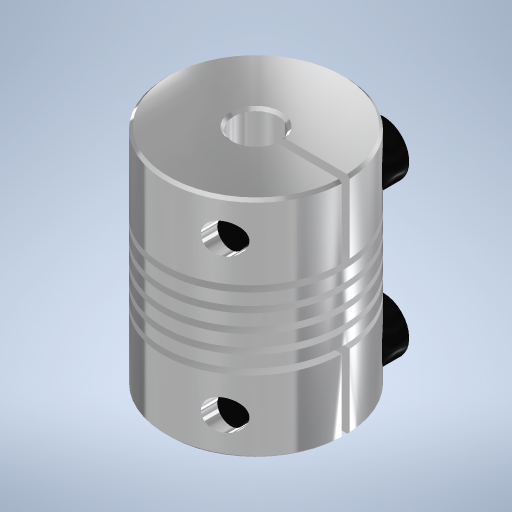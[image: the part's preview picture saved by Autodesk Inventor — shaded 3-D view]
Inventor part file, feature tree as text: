
AUTODESK INVENTOR PART (.ipt)
format: ipt  version: 2024 (Build 280153000, 153)  size: 555,520 bytes
history: native  units: mm
features: extrude x3, sketch x3, projected_geometry x2, chamfer x1, other x1, fillet x1, pattern_linear x1, imported_body x1
ambient origin geometry x8: Origin, YZ Plane, XZ Plane, XY Plane, X Axis, Y Axis, Z Axis, Center Point
bodies: Solid2 (feature_tree)
feature tree (13):
  chamfer  "Chamfer1"  Distance=3.0mm
  other  "Flexible Coupling 5mm x 8mm1"
  extrude  "Extrusion1"  Depth=3.0mm TaperAngle=0.0deg
  extrude  "Extrusion2"  Depth=0.25mm TaperAngle=0.0deg
  extrude  "Extrusion3"  Depth=0.25mm
  fillet  "Fillet1"  Radius=20.0mm
  pattern_linear  "Rectangular Pattern1"  [2 undecoded]
  imported_body  "Base1"
  sketch  "Sketch1"  dims[d0=6.0mm d1=3.0mm d2=0.0mm]
  projected_geometry  "Projected Loop1"
  sketch  "Sketch2"  dims[d3=3.0mm d4=2.0mm d5=0.0mm]
  sketch  "Sketch3"  dims[d6=3.0mm d7=14.0mm d8=0.0mm d9=0.25mm d10=20.0mm d12=17.0mm]
  projected_geometry  "Projected Loop2"
note: 2 required parameter values undecoded (feature->parameter linkage not recoverable at this tier; creation-order binding heuristic only, values carry confidence <= 0.55)
